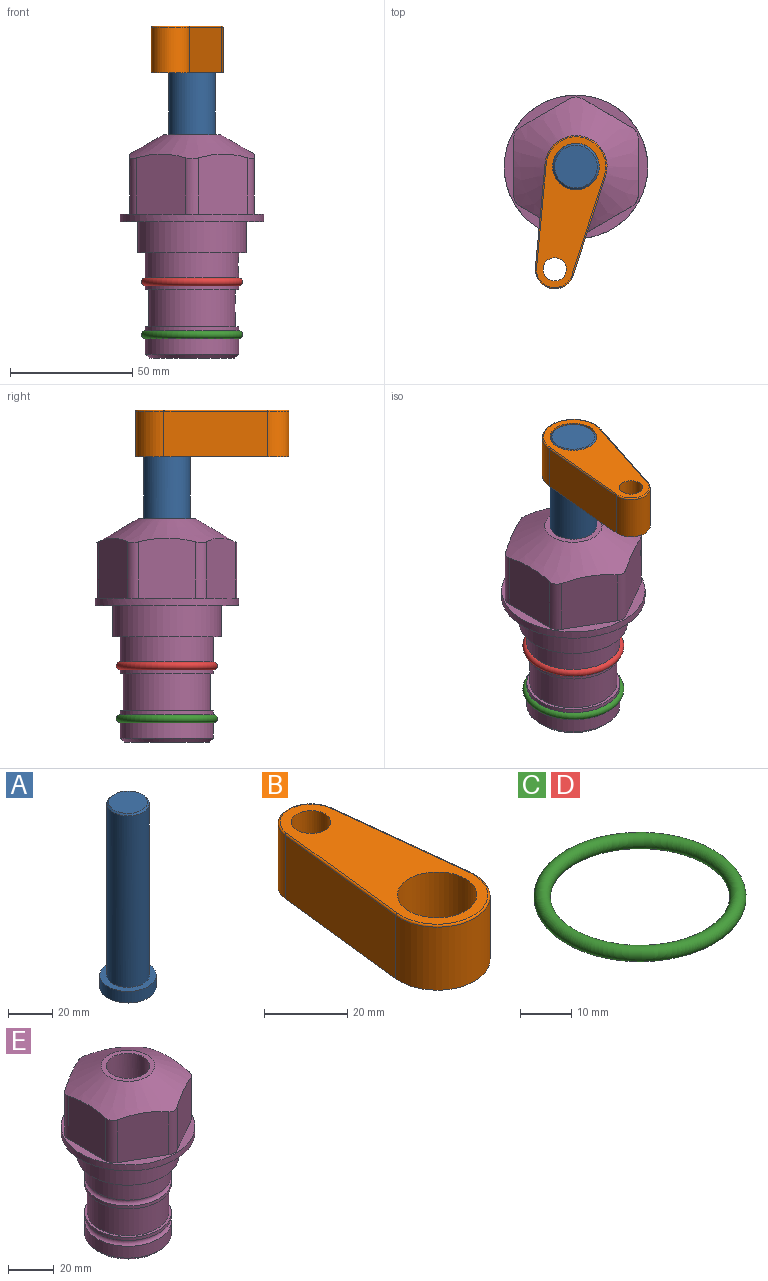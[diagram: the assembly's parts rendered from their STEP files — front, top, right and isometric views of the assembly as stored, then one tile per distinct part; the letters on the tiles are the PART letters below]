
ASSEMBLY  parts=5 mates=3
PART A: 6 faces, bbox 25.4x25.4x101.6 mm
  f0: plane 17.46x17.46mm, normal (0,0,1), area 239.5mm2, adj f5
  f1: plane 25.4x25.4mm, normal (0,0,-1), area 506.7mm2, adj f2
  f2: cylinder r=12.7mm len=25.4mm, axis (0,0,1), area 506.7mm2, adj f1,f3
  f3: plane 25.4x25.4mm, normal (0,0,1), area 221.7mm2, adj f2,f4
  f4: cylinder r=9.53mm len=94.46mm, axis (0,0,1), area 5653mm2, adj f3,f5
  f5: cone r=8.73mm half-angle=45deg, axis (0,0,-1), area 64.4mm2, adj f0,f4
PART B: 29 faces, bbox 27.5x65.2x19.1 mm
  f0: plane 63.5x25.4mm, normal (0,0,-1), area 561.7mm2, adj f1,f2,f3,f4,f5,f6,f12,f13
  f1: cylinder r=12.7mm len=25.4mm, axis (0,0,-1), area 792.2mm2, adj f0,f2,f4,f9
  f2: plane 42.33x18.54mm, normal (0.99,0.11,0), area 789.8mm2, adj f0,f1,f3,f8
  f3: cylinder r=7.94mm len=18.54mm, axis (0,0,-1), area 429.6mm2, adj f0,f2,f4,f10
  f4: plane 42.33x18.54mm, normal (-0.99,0.11,0), area 789.8mm2, adj f0,f1,f3,f11
  f5: cylinder r=9.53mm len=19.05mm, axis (0,0,-1), area 1140.1mm2, adj f0,f7
  f6: cylinder r=4.76mm len=19.05mm, axis (0,0,-1), area 570mm2, adj f0,f7
  f7: plane 62.48x24.38mm, normal (0,0,1), area 810.1mm2, adj f5,f6,f8,f9,f10,f11
  f8: cylinder r=0.51mm len=42.39mm, axis (0.11,-0.99,0), area 34mm2, adj f2,f7,f9,f10
  f9: torus R=12.19mm, axis (0,0,1), area 33.6mm2, adj f1,f7,f8,f11
  f10: torus R=7.43mm, axis (0,0,1), area 18.1mm2, adj f3,f7,f8,f11
  f11: cylinder r=0.51mm len=42.39mm, axis (0.11,0.99,0), area 34mm2, adj f4,f7,f9,f10
  f12: plane 21.6x14.29mm, normal (-0.99,-0.11,0), area 310.6mm2, adj f0,f17,f19,f23
  f13: plane 21.6x14.29mm, normal (0.99,-0.11,0), area 310.6mm2, adj f0,f18,f20,f26
  f14: cylinder r=12.7mm len=14.29mm, axis (0,0,-1), area 173.4mm2, adj f0,f17,f18,f22
  f15: cylinder r=7.94mm len=14.29mm, axis (0,0,-1), area 102.3mm2, adj f0,f19,f20,f27
  f16: plane 21.6x13.14mm, normal (0,0,-1), area 212.1mm2, adj f22,f23,f26,f27
  f17: cylinder r=1.59mm len=14.29mm, axis (0,0,-1), area 49mm2, adj f0,f12,f14,f21
  f18: cylinder r=1.59mm len=14.29mm, axis (0,0,-1), area 49mm2, adj f0,f13,f14,f24
  f19: cylinder r=1.59mm len=14.29mm, axis (0,0,-1), area 43.3mm2, adj f0,f12,f15,f25
  f20: cylinder r=1.59mm len=14.29mm, axis (0,0,-1), area 43.3mm2, adj f0,f13,f15,f28
  f21: sphere r=1.59mm, area 5.4mm2, adj f17,f22,f23
  f22: torus R=14.29mm, axis (0,0,1), area 31.6mm2, adj f14,f16,f21,f24
  f23: cylinder r=1.59mm len=21.78mm, axis (0.11,-0.99,0), area 54.2mm2, adj f12,f16,f21,f25
  f24: sphere r=1.59mm, area 5.4mm2, adj f18,f22,f26
  f25: sphere r=1.59mm, area 4.8mm2, adj f19,f23,f27
  f26: cylinder r=1.59mm len=21.78mm, axis (0.11,0.99,0), area 54.2mm2, adj f13,f16,f24,f28
  f27: torus R=9.53mm, axis (0,0,1), area 19.2mm2, adj f15,f16,f25,f28
  f28: sphere r=1.59mm, area 4.8mm2, adj f20,f26,f27
PART C: 1 faces, bbox 44.7x44.7x3.2 mm
  f0: torus R=19.05mm, axis (0,0,1), area 1193.9mm2
PART D: same geometry as C
PART E: 36 faces, bbox 58.7x58.7x91.2 mm
  f0: cylinder r=17.78mm len=35.56mm, axis (0,0,1), area 1670.8mm2, adj f23,f24,f31
  f1: cylinder r=19.05mm len=38.1mm, axis (0,0,1), area 1191.9mm2, adj f26,f27,f30
  f2: plane 58.66x58.66mm, normal (0,0,-1), area 1150.6mm2, adj f3,f28
  f3: cylinder r=29.33mm len=58.66mm, axis (0,0,-1), area 585.1mm2, adj f2,f4
  f4: plane 58.66x58.66mm, normal (0,0,1), area 475.9mm2, adj f3,f5,f6,f7,f8,f9,f10,f11
  f5: plane 24.5x20.32mm, normal (-0.5,0.87,0), area 562.8mm2, adj f4,f15,f16,f17
  f6: plane 24.5x20.32mm, normal (0.5,0.87,0), area 562.8mm2, adj f4,f14,f15,f17
  f7: plane 24.5x23.48mm, normal (1,0,0), area 562.8mm2, adj f4,f13,f14,f17
  f8: plane 24.5x20.32mm, normal (0.5,-0.87,0), area 562.8mm2, adj f4,f12,f13,f17
  f9: plane 24.5x20.32mm, normal (-0.5,-0.87,0), area 562.8mm2, adj f4,f11,f12,f17
  f10: plane 24.5x23.48mm, normal (-1,0,0), area 562.8mm2, adj f4,f11,f16,f17
  f11: cylinder r=5.08mm len=23.01mm, axis (0,0,-1), area 121.2mm2, adj f4,f9,f10,f17
  f12: cylinder r=5.08mm len=23.01mm, axis (0,0,-1), area 121.2mm2, adj f4,f8,f9,f17
  f13: cylinder r=5.08mm len=23.01mm, axis (0,0,-1), area 121.2mm2, adj f4,f7,f8,f17
  f14: cylinder r=5.08mm len=23.01mm, axis (0,0,-1), area 121.2mm2, adj f4,f6,f7,f17
  f15: cylinder r=5.08mm len=23.01mm, axis (0,0,-1), area 121.2mm2, adj f4,f5,f6,f17
  f16: cylinder r=5.08mm len=23.01mm, axis (0,0,-1), area 121.2mm2, adj f4,f5,f10,f17
  f17: cone r=11.73mm half-angle=60deg, axis (0,0,-1), area 2071.8mm2, adj f5,f6,f7,f8,f9,f10,f11,f12
  f18: plane 23.46x23.46mm, normal (0,0,1), area 147.4mm2, adj f17,f35
  f19: plane 34.93x34.93mm, normal (0,0,-1), area 958mm2, adj f29
  f20: cylinder r=19.05mm len=38.1mm, axis (0,0,1), area 760.1mm2, adj f21,f29
  f21: torus R=19.05mm, axis (0,0,1), area 565.3mm2, adj f20,f22
  f22: cylinder r=19.05mm len=38.1mm, axis (0,0,1), area 190mm2, adj f21,f23
  f23: plane 38.1x38.1mm, normal (0,0,1), area 146.9mm2, adj f0,f22
  f24: plane 38.1x38.1mm, normal (0,0,-1), area 146.9mm2, adj f0,f25
  f25: cylinder r=19.05mm len=38.1mm, axis (0,0,1), area 190mm2, adj f24,f26
  f26: torus R=19.05mm, axis (0,0,1), area 565.3mm2, adj f1,f25
  f27: plane 44.45x44.45mm, normal (0,0,-1), area 411.7mm2, adj f1,f28
  f28: cylinder r=22.23mm len=44.45mm, axis (0,0,1), area 1773.5mm2, adj f2,f27
  f29: cone r=19.05mm half-angle=45deg, axis (0,0,1), area 257.5mm2, adj f19,f20
  f30: cylinder r=3.17mm len=6.75mm, axis (-1,0,0), area 128mm2, adj f1,f33
  f31: cylinder r=3.17mm len=6.35mm, axis (-1,0,0), area 102.5mm2, adj f0,f33
  f32: plane 25.4x25.4mm, normal (0,0,1), area 506.7mm2, adj f33
  f33: cylinder r=12.7mm len=66.42mm, axis (0,0,-1), area 5236.2mm2, adj f30,f31,f32,f34
  f34: cone r=9.53mm half-angle=30deg, axis (0,0,-1), area 443.4mm2, adj f33,f35
  f35: cylinder r=9.53mm len=19.05mm, axis (0,0,-1), area 849mm2, adj f18,f34
PLACE A rot(axis=(0,0,-1),101.7deg) t=(0,0,6.38)mm
PLACE B rot(axis=(0,0,1),168.3deg) t=(0,0,60.99)mm
PLACE C t=(0,0,-21.59)mm
PLACE D at identity
PLACE E at identity fixed
MATE fastened C.f0 <-> E.f0  axis (0,0,1) through (0,0,-46.1)mm
MATE cylindrical A.f2 <-> E.f0  axis (0,0,1) through (0,0,32.01)mm
MATE fastened B.f1 <-> A.f2  axis (0,0,1) through (0,0,80.04)mm
